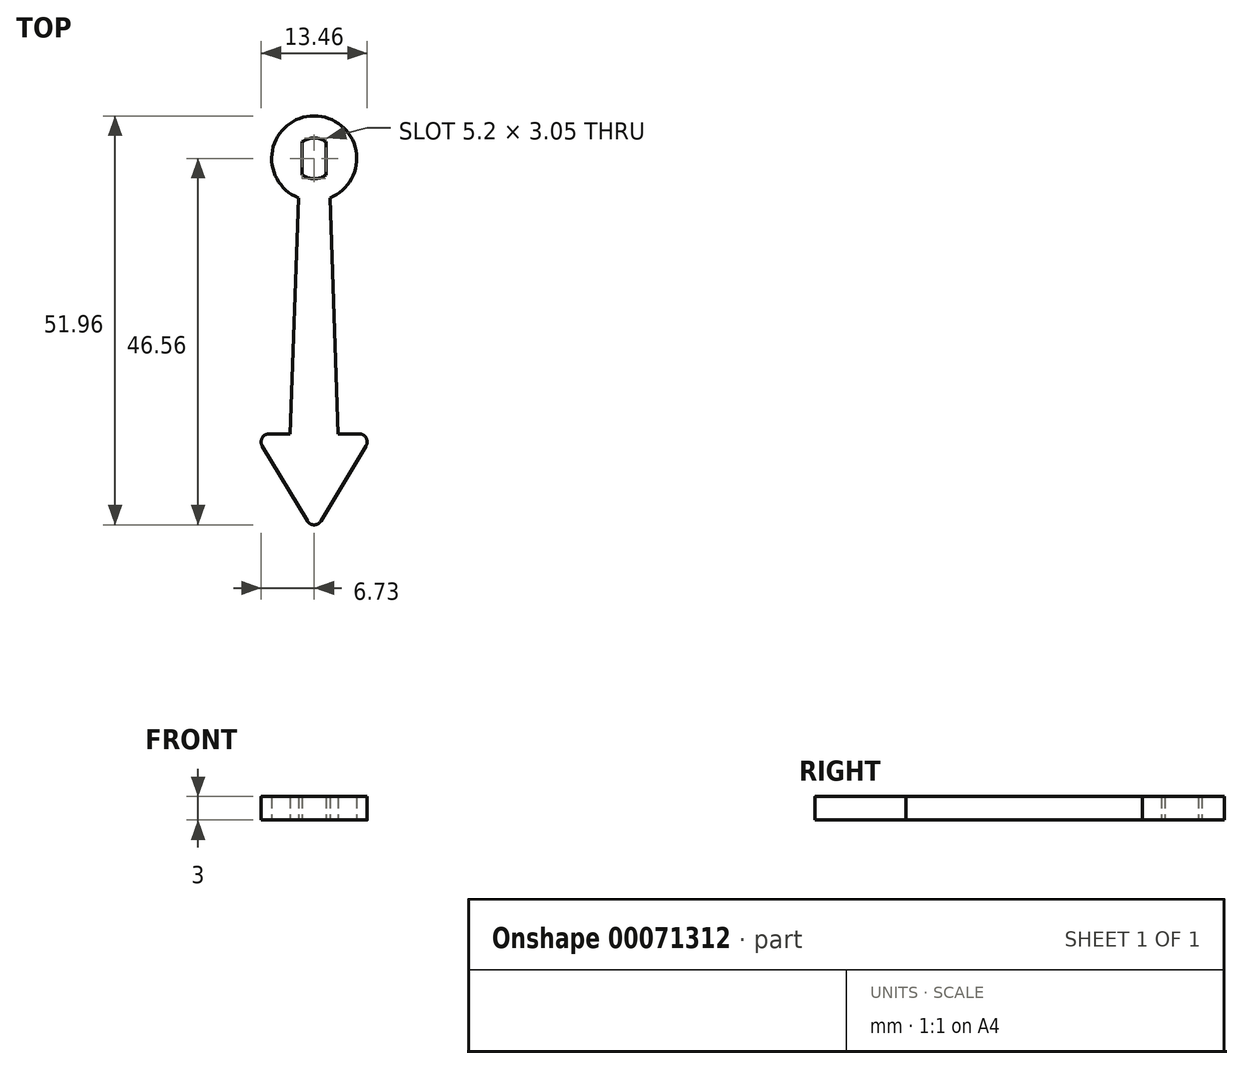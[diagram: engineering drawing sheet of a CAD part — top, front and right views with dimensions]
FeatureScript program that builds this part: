
annotation { "Feature Type Name" : "Feature", "Feature Type Description" : "" }
export const myFeature = defineFeature(function(context is Context, id is Id, definition is map)
    precondition{}
    {
        {
            var Q0;
            Q0=qCreatedBy(makeId("Top.planeOp"),FACE);
            var sketch = newSketch(context, id + "F0", { "sketchPlane" : qUnion([Q0])});
            skCircle(sketch, "E0", {"center": v(0, 0) * mm, "radius": 5.4 * mm});
            skCircle(sketch, "E1", {"center": v(0, 0) * mm, "radius": 2.6 * mm});
            skLineSegment(sketch, "E2", {"start": v(-1.52, -2.1) * mm, "end": v(-1.52, 2.1) * mm});
            skLineSegment(sketch, "E3", {"start": v(1.53, -2.1) * mm, "end": v(1.53, 2.1) * mm});
            skSolve(sketch);
        }
        {
            var Q0;
            {var subQ0=sQuery(id+"F0.wireOp",EDGE,"E3");Q0=makeQuery(id+"F0.imprint","IMPRINT",FACE,{"disambiguationData":[TD([[makeQuery(id+"F0.imprint","IMPRINT",EDGE,{"derivedFrom":subQ0}),-1.0]])]});}
            var Q1;
            {var subQ0=sQuery(id+"F0.wireOp",EDGE,"E2");Q1=makeQuery(id+"F0.imprint","IMPRINT",FACE,{"disambiguationData":[TD([[makeQuery(id+"F0.imprint","IMPRINT",EDGE,{"derivedFrom":subQ0}),1.0]])]});}
            var Q2;
            Q2=makeQuery(id+"F0.imprint","IMPRINT",FACE,{"disambiguationData":[TD([[makeQuery(id+"F0.imprint","IMPRINT",EDGE,{"derivedFrom":sQuery(id+"F0.wireOp",EDGE,"E0")}),1.0]])]});
            extrude(context, id + "F1", {"entities" : qUnion([Q0, Q1, Q2]), "endBound" : BoundingType.SYMMETRIC, "depth" : 3 * mm});
        }
        {
            var Q0;
            Q0=makeQuery(id+"F1.opExtrude","CAP_FACE",FACE,{"disambiguationData":[OSD([sQuery(id+"F0.wireOp",EDGE,"E0"),sQuery(id+"F0.wireOp",EDGE,"E1"),sQuery(id+"F0.wireOp",EDGE,"E2"),sQuery(id+"F0.wireOp",EDGE,"E3")])],"isStart":true});
            var sketch = newSketch(context, id + "F2", { "sketchPlane" : qUnion([Q0])});
            skLineSegment(sketch, "E4", {"start": v(0, 0) * mm, "end": v(0, 35) * mm});
            skLineSegment(sketch, "E5", {"start": v(0, 35) * mm, "end": v(3.05, 35) * mm});
            skLineSegment(sketch, "E6", {"start": v(0, 5.02) * mm, "end": v(2, 5.02) * mm});
            skLineSegment(sketch, "E7", {"start": v(2, 5.02) * mm, "end": v(3.05, 35) * mm});
            skLineSegment(sketch, "E8.MirrorCS", {"start": v(-2, 5.02) * mm, "end": v(-3.05, 35) * mm});
            skLineSegment(sketch, "E9.MirrorCS", {"start": v(0, 35) * mm, "end": v(-3.05, 35) * mm});
            skLineSegment(sketch, "E10.MirrorCS", {"start": v(0, 5.02) * mm, "end": v(-2, 5.02) * mm});
            skLineSegment(sketch, "E11", {"start": v(0, 35) * mm, "end": v(0, 47.5) * mm});
            skLineSegment(sketch, "E12", {"start": v(-7.5, 35) * mm, "end": v(7.5, 35) * mm});
            skLineSegment(sketch, "E13", {"start": v(0, 47.5) * mm, "end": v(7.5, 35) * mm});
            skLineSegment(sketch, "E14.MirrorCS", {"start": v(0, 47.5) * mm, "end": v(-7.5, 35) * mm});
            skSolve(sketch);
        }
        {
            var Q0;
            Q0 = qSketchRegion(id + "F2", true);
            var Q1;
            Q1=makeQuery(id+"F1.opExtrude","CAP_FACE",FACE,{"disambiguationData":[OSD([sQuery(id+"F0.wireOp",EDGE,"E0"),sQuery(id+"F0.wireOp",EDGE,"E1"),sQuery(id+"F0.wireOp",EDGE,"E2"),sQuery(id+"F0.wireOp",EDGE,"E3")])],"isStart":false});
            extrude(context, id + "F3", {"entities" : qUnion([Q0]), "operationType" : NewBodyOperationType.ADD, "endBound" : BoundingType.UP_TO_SURFACE, "oppositeDirection" : true, "endBoundEntityFace" : qUnion([Q1]), "depth" : 25 * mm});
        }
        {
            var Q0;
            Q0=makeQuery(id+"F3.opExtrude","SWEPT_EDGE",EDGE,{"disambiguationData":[OSD([sQuery(id+"F2.wireOp",EDGE,"E11"),sQuery(id+"F2.wireOp",EDGE,"E13"),sQuery(id+"F2.wireOp",EDGE,"E14.MirrorCS")])]});
            var Q1;
            Q1=makeQuery(id+"F3.opExtrude","SWEPT_EDGE",EDGE,{"disambiguationData":[OSD([sQuery(id+"F2.wireOp",EDGE,"E12"),sQuery(id+"F2.wireOp",EDGE,"E14.MirrorCS")])]});
            var Q2;
            Q2=makeQuery(id+"F3.opExtrude","SWEPT_EDGE",EDGE,{"disambiguationData":[OSD([sQuery(id+"F2.wireOp",EDGE,"E12"),sQuery(id+"F2.wireOp",EDGE,"E13")])]});
            fillet(context, id + "F4", {"entities" : qUnion([Q0, Q1, Q2]), "radius" : 1 * mm, "tangentPropagation" : true, "allowEdgeOverflow" : false});
        }
    });
